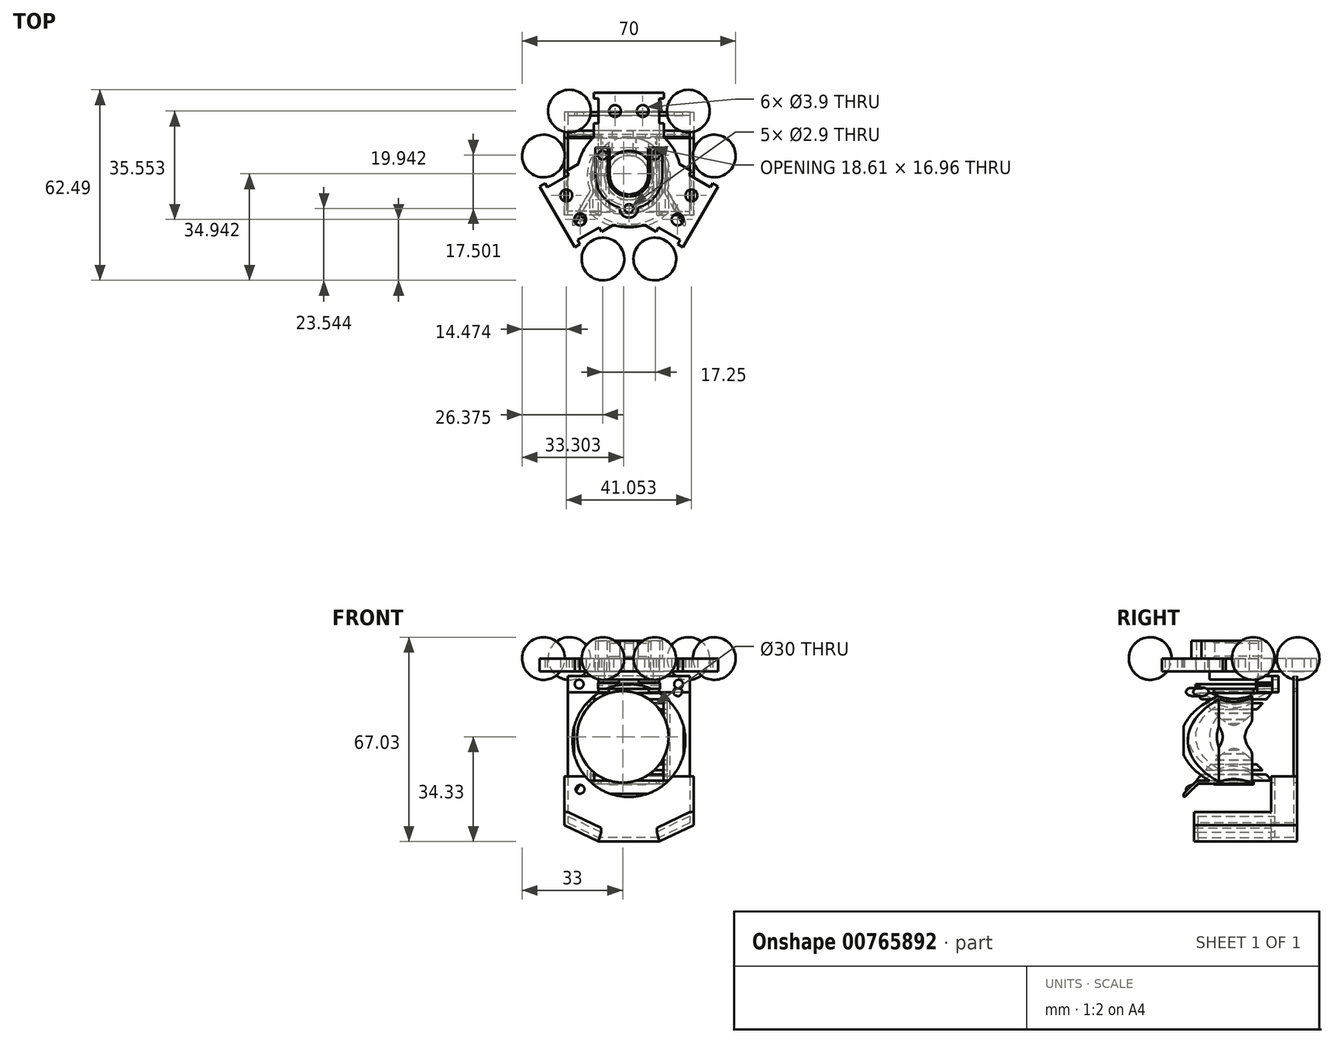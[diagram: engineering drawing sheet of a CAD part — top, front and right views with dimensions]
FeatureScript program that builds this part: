
annotation { "Feature Type Name" : "Feature", "Feature Type Description" : "" }
export const myFeature = defineFeature(function(context is Context, id is Id, definition is map)
    precondition{}
    {
        {
            var Q0;
            Q0=qCreatedBy(makeId("Top.planeOp"),FACE);
            var sketch = newSketch(context, id + "F0", { "sketchPlane" : qUnion([Q0])});
            skCircle(sketch, "E0", {"center": v(0, 0) * mm, "radius": 8.07 * mm});
            skCircle(sketch, "E1", {"center": v(0, 0) * mm, "radius": 17 * mm});
            skLineSegment(sketch, "E2.bottom", {"start": v(-11.5, 17) * mm, "end": v(11.5, 17) * mm});
            skLineSegment(sketch, "E2.top", {"start": v(-11.5, 12.52) * mm, "end": v(11.5, 12.52) * mm});
            skLineSegment(sketch, "E2.left", {"start": v(-11.5, 17) * mm, "end": v(-11.5, 12.52) * mm});
            skLineSegment(sketch, "E2.right", {"start": v(11.5, 17) * mm, "end": v(11.5, 12.52) * mm});
            skLineSegment(sketch, "E3.bottom", {"start": v(-11.5, 27.15) * mm, "end": v(11.5, 27.15) * mm});
            skLineSegment(sketch, "E3.top", {"start": v(-11.5, 25.15) * mm, "end": v(11.5, 25.15) * mm});
            skLineSegment(sketch, "E3.left", {"start": v(-11.5, 27.15) * mm, "end": v(-11.5, 25.15) * mm});
            skLineSegment(sketch, "E3.right", {"start": v(11.5, 27.15) * mm, "end": v(11.5, 25.15) * mm});
            skLineSegment(sketch, "E4.bottom", {"start": v(-9.95, 25.15) * mm, "end": v(9.95, 25.15) * mm});
            skLineSegment(sketch, "E4.top", {"start": v(-9.95, 17) * mm, "end": v(9.95, 17) * mm});
            skLineSegment(sketch, "E4.left", {"start": v(-9.95, 25.15) * mm, "end": v(-9.95, 17) * mm});
            skLineSegment(sketch, "E4.right", {"start": v(9.95, 25.15) * mm, "end": v(9.95, 17) * mm});
            skCircle(sketch, "E5", {"center": v(-4.55, 21.08) * mm, "radius": 1.95 * mm});
            skPoint(sketch, "E6", {"position": v(-9.95, 21.08) * mm});
            skCircle(sketch, "E7.MirrorC", {"center": v(4.55, 21.08) * mm, "radius": 1.95 * mm});
            skLineSegment(sketch, "E8.1.0", {"start": v(-17.76, -23.53) * mm, "end": v(-29.26, -3.62) * mm});
            skLineSegment(sketch, "E8.1.1", {"start": v(-20.47, 1.46) * mm, "end": v(-16.6, 3.7) * mm});
            skCircle(sketch, "E8.1.2", {"center": v(-20.53, -6.6) * mm, "radius": 1.95 * mm});
            skLineSegment(sketch, "E8.1.3", {"start": v(-8.97, -18.46) * mm, "end": v(-5.1, -16.22) * mm});
            skLineSegment(sketch, "E8.1.4", {"start": v(-5.1, -16.22) * mm, "end": v(-16.6, 3.7) * mm});
            skLineSegment(sketch, "E8.1.5", {"start": v(-16.8, -21.2) * mm, "end": v(-26.76, -3.96) * mm});
            skCircle(sketch, "E8.1.6", {"center": v(-15.98, -14.48) * mm, "radius": 1.95 * mm});
            skLineSegment(sketch, "E8.1.7", {"start": v(-26.76, -3.96) * mm, "end": v(-19.7, 0.12) * mm});
            skLineSegment(sketch, "E8.1.8", {"start": v(-16.8, -21.2) * mm, "end": v(-9.75, -17.12) * mm});
            skLineSegment(sketch, "E8.1.9", {"start": v(-9.75, -17.12) * mm, "end": v(-19.7, 0.12) * mm});
            skPoint(sketch, "E8.1.10", {"position": v(-13.28, -19.15) * mm});
            skLineSegment(sketch, "E8.1.11", {"start": v(-16.03, -22.53) * mm, "end": v(-27.53, -2.62) * mm});
            skLineSegment(sketch, "E8.1.12", {"start": v(-8.97, -18.46) * mm, "end": v(-20.47, 1.46) * mm});
            skLineSegment(sketch, "E8.1.13", {"start": v(-17.76, -23.53) * mm, "end": v(-16.03, -22.53) * mm});
            skLineSegment(sketch, "E8.1.14", {"start": v(-29.26, -3.62) * mm, "end": v(-27.53, -2.62) * mm});
            skLineSegment(sketch, "E8.2.0", {"start": v(29.26, -3.62) * mm, "end": v(17.76, -23.53) * mm});
            skLineSegment(sketch, "E8.2.1", {"start": v(8.97, -18.46) * mm, "end": v(5.1, -16.22) * mm});
            skCircle(sketch, "E8.2.2", {"center": v(15.98, -14.48) * mm, "radius": 1.95 * mm});
            skLineSegment(sketch, "E8.2.3", {"start": v(20.47, 1.46) * mm, "end": v(16.6, 3.7) * mm});
            skLineSegment(sketch, "E8.2.4", {"start": v(16.6, 3.7) * mm, "end": v(5.1, -16.22) * mm});
            skLineSegment(sketch, "E8.2.5", {"start": v(26.76, -3.96) * mm, "end": v(16.8, -21.2) * mm});
            skCircle(sketch, "E8.2.6", {"center": v(20.53, -6.6) * mm, "radius": 1.95 * mm});
            skLineSegment(sketch, "E8.2.7", {"start": v(16.8, -21.2) * mm, "end": v(9.75, -17.12) * mm});
            skLineSegment(sketch, "E8.2.8", {"start": v(26.76, -3.96) * mm, "end": v(19.7, 0.12) * mm});
            skLineSegment(sketch, "E8.2.9", {"start": v(19.7, 0.12) * mm, "end": v(9.75, -17.12) * mm});
            skPoint(sketch, "E8.2.10", {"position": v(23.23, -1.92) * mm});
            skLineSegment(sketch, "E8.2.11", {"start": v(27.53, -2.62) * mm, "end": v(16.03, -22.53) * mm});
            skLineSegment(sketch, "E8.2.12", {"start": v(20.47, 1.46) * mm, "end": v(8.97, -18.46) * mm});
            skLineSegment(sketch, "E8.2.13", {"start": v(29.26, -3.62) * mm, "end": v(27.53, -2.62) * mm});
            skLineSegment(sketch, "E8.2.14", {"start": v(17.76, -23.53) * mm, "end": v(16.03, -22.53) * mm});
            skSolve(sketch);
        }
        {
            var Q0;
            Q0 = qSketchRegion(id + "F0", true);
            extrude(context, id + "F1", {"entities" : qUnion([Q0]), "depth" : 4.2 * mm, "offsetDistance" : 25 * mm});
        }
        {
            var Q0;
            Q0=makeQuery(id+"F1.opExtrude","CAP_FACE",FACE,{"disambiguationData":[OSD([sQuery(id+"F0.wireOp",EDGE,"E0"),sQuery(id+"F0.wireOp",EDGE,"E1"),sQuery(id+"F0.wireOp",EDGE,"E2.bottom"),sQuery(id+"F0.wireOp",EDGE,"E2.left"),sQuery(id+"F0.wireOp",EDGE,"E2.right"),sQuery(id+"F0.wireOp",EDGE,"E3.bottom"),sQuery(id+"F0.wireOp",EDGE,"E3.top"),sQuery(id+"F0.wireOp",EDGE,"E3.left"),sQuery(id+"F0.wireOp",EDGE,"E3.right"),sQuery(id+"F0.wireOp",EDGE,"E4.left"),sQuery(id+"F0.wireOp",EDGE,"E4.right"),sQuery(id+"F0.wireOp",EDGE,"E5"),sQuery(id+"F0.wireOp",EDGE,"E7.MirrorC"),sQuery(id+"F0.wireOp",EDGE,"E8.1.0"),sQuery(id+"F0.wireOp",EDGE,"E8.1.1"),sQuery(id+"F0.wireOp",EDGE,"E8.1.2"),sQuery(id+"F0.wireOp",EDGE,"E8.1.3"),sQuery(id+"F0.wireOp",EDGE,"E8.1.6"),sQuery(id+"F0.wireOp",EDGE,"E8.1.7"),sQuery(id+"F0.wireOp",EDGE,"E8.1.8"),sQuery(id+"F0.wireOp",EDGE,"E8.1.11"),sQuery(id+"F0.wireOp",EDGE,"E8.1.12"),sQuery(id+"F0.wireOp",EDGE,"E8.1.13"),sQuery(id+"F0.wireOp",EDGE,"E8.1.14"),sQuery(id+"F0.wireOp",EDGE,"E8.2.0"),sQuery(id+"F0.wireOp",EDGE,"E8.2.1"),sQuery(id+"F0.wireOp",EDGE,"E8.2.2"),sQuery(id+"F0.wireOp",EDGE,"E8.2.3"),sQuery(id+"F0.wireOp",EDGE,"E8.2.6"),sQuery(id+"F0.wireOp",EDGE,"E8.2.7"),sQuery(id+"F0.wireOp",EDGE,"E8.2.8"),sQuery(id+"F0.wireOp",EDGE,"E8.2.11"),sQuery(id+"F0.wireOp",EDGE,"E8.2.12"),sQuery(id+"F0.wireOp",EDGE,"E8.2.13"),sQuery(id+"F0.wireOp",EDGE,"E8.2.14")])],"isStart":false});
            var sketch = newSketch(context, id + "F2", { "sketchPlane" : qUnion([Q0])});
            skArc(sketch, "E9.0", {"start": v(-8.07, 0) * mm, "mid": v(0, -8.07) * mm, "end": v(8.07, 0) * mm, "construction": true});
            skArc(sketch, "E10.0", {"start": v(-11, 0) * mm, "mid": v(0, -11) * mm, "end": v(11, 0) * mm});
            skLineSegment(sketch, "E11", {"start": v(-11, 0) * mm, "end": v(11, 0) * mm, "construction": true});
            skArc(sketch, "E12", {"start": v(-6.25, 0) * mm, "mid": v(0, -6.25) * mm, "end": v(6.25, 0) * mm});
            skLineSegment(sketch, "E13.bottom", {"start": v(-11, 0) * mm, "end": v(-6.25, 0) * mm});
            skLineSegment(sketch, "E13.top", {"start": v(-11, 9) * mm, "end": v(-6.25, 9) * mm});
            skLineSegment(sketch, "E13.left", {"start": v(-11, 0) * mm, "end": v(-11, 9) * mm});
            skLineSegment(sketch, "E13.right", {"start": v(-6.25, 0) * mm, "end": v(-6.25, 9) * mm});
            skLineSegment(sketch, "E14.MirrorCS", {"start": v(11, 0) * mm, "end": v(11, 9) * mm});
            skLineSegment(sketch, "E15.MirrorCS", {"start": v(6.25, 0) * mm, "end": v(6.25, 9) * mm});
            skLineSegment(sketch, "E16.MirrorCS", {"start": v(11, 9) * mm, "end": v(6.25, 9) * mm});
            skCircle(sketch, "E17", {"center": v(8.62, 6.63) * mm, "radius": 1.45 * mm});
            skPoint(sketch, "E17.centerSnap0", {"position": v(8.62, 9) * mm});
            skCircle(sketch, "E18", {"center": v(8.62, 6.63) * mm, "radius": 2.37 * mm, "construction": true});
            skCircle(sketch, "E19.MirrorC", {"center": v(-8.62, 6.63) * mm, "radius": 1.45 * mm});
            skCircle(sketch, "E20", {"center": v(0, 0) * mm, "radius": 10.88 * mm, "construction": true});
            skCircle(sketch, "E21", {"center": v(0, -10.88) * mm, "radius": 1.45 * mm});
            skPoint(sketch, "E21.centerSnap0", {"position": v(0, -11) * mm});
            skCircle(sketch, "E22", {"center": v(0, -10.88) * mm, "radius": 3 * mm});
            skSolve(sketch);
        }
        {
            var Q0;
            Q0 = qSketchRegion(id + "F2", true);
            extrude(context, id + "F3", {"entities" : qUnion([Q0]), "depth" : 5.8 * mm, "offsetDistance" : 25 * mm});
        }
        {
            var Q0;
            Q0=makeQuery(id+"F2.imprint","IMPRINT",FACE,{"disambiguationData":[TD([[makeQuery(id+"F2.imprint","IMPRINT",EDGE,{"derivedFrom":sQuery(id+"F2.wireOp",EDGE,"E19.MirrorC")}),-1.0]])]});
            var Q1;
            Q1=makeQuery(id+"F2.imprint","IMPRINT",FACE,{"disambiguationData":[TD([[makeQuery(id+"F2.imprint","IMPRINT",EDGE,{"derivedFrom":sQuery(id+"F2.wireOp",EDGE,"E17")}),1.0]])]});
            var Q2;
            {var subQ0=sQuery(id+"F2.wireOp",EDGE,"E21");var subQ1=sQuery(id+"F2.wireOp",EDGE,"E10.0");var subQ2=makeQuery(id+"F2.imprint","INTERSECT",VERTEX,{"disambiguationData":[OD(0.0)],"derivedFrom":[subQ1,subQ0]});Q2=makeQuery(id+"F2.imprint","IMPRINT",FACE,{"disambiguationData":[TD([[makeQuery(id+"F2.imprint","IMPRINT",EDGE,{"disambiguationData":[TD([[subQ2,-1.0]])],"derivedFrom":subQ1}),1.0]])]});}
            var Q3;
            {var subQ0=sQuery(id+"F2.wireOp",EDGE,"E21");var subQ1=sQuery(id+"F2.wireOp",EDGE,"E10.0");var subQ2=makeQuery(id+"F2.imprint","INTERSECT",VERTEX,{"disambiguationData":[OD(0.0)],"derivedFrom":[subQ1,subQ0]});Q3=makeQuery(id+"F2.imprint","IMPRINT",FACE,{"disambiguationData":[TD([[makeQuery(id+"F2.imprint","IMPRINT",EDGE,{"disambiguationData":[TD([[subQ2,-1.0]])],"derivedFrom":subQ1}),-1.0]])]});}
            extrude(context, id + "F4", {"entities" : qUnion([Q0, Q1, Q2, Q3]), "operationType" : NewBodyOperationType.REMOVE, "endBound" : BoundingType.THROUGH_ALL, "oppositeDirection" : true, "depth" : 25 * mm, "offsetDistance" : 25 * mm});
        }
        {
            var Q0;
            Q0=makeQuery(id+"F1.opExtrude","CAP_FACE",FACE,{"disambiguationData":[OSD([sQuery(id+"F0.wireOp",EDGE,"E0"),sQuery(id+"F0.wireOp",EDGE,"E1"),sQuery(id+"F0.wireOp",EDGE,"E2.bottom"),sQuery(id+"F0.wireOp",EDGE,"E2.left"),sQuery(id+"F0.wireOp",EDGE,"E2.right"),sQuery(id+"F0.wireOp",EDGE,"E3.bottom"),sQuery(id+"F0.wireOp",EDGE,"E3.top"),sQuery(id+"F0.wireOp",EDGE,"E3.left"),sQuery(id+"F0.wireOp",EDGE,"E3.right"),sQuery(id+"F0.wireOp",EDGE,"E4.left"),sQuery(id+"F0.wireOp",EDGE,"E4.right"),sQuery(id+"F0.wireOp",EDGE,"E5"),sQuery(id+"F0.wireOp",EDGE,"E7.MirrorC"),sQuery(id+"F0.wireOp",EDGE,"E8.1.0"),sQuery(id+"F0.wireOp",EDGE,"E8.1.1"),sQuery(id+"F0.wireOp",EDGE,"E8.1.2"),sQuery(id+"F0.wireOp",EDGE,"E8.1.3"),sQuery(id+"F0.wireOp",EDGE,"E8.1.6"),sQuery(id+"F0.wireOp",EDGE,"E8.1.7"),sQuery(id+"F0.wireOp",EDGE,"E8.1.8"),sQuery(id+"F0.wireOp",EDGE,"E8.1.11"),sQuery(id+"F0.wireOp",EDGE,"E8.1.12"),sQuery(id+"F0.wireOp",EDGE,"E8.1.13"),sQuery(id+"F0.wireOp",EDGE,"E8.1.14"),sQuery(id+"F0.wireOp",EDGE,"E8.2.0"),sQuery(id+"F0.wireOp",EDGE,"E8.2.1"),sQuery(id+"F0.wireOp",EDGE,"E8.2.2"),sQuery(id+"F0.wireOp",EDGE,"E8.2.3"),sQuery(id+"F0.wireOp",EDGE,"E8.2.6"),sQuery(id+"F0.wireOp",EDGE,"E8.2.7"),sQuery(id+"F0.wireOp",EDGE,"E8.2.8"),sQuery(id+"F0.wireOp",EDGE,"E8.2.11"),sQuery(id+"F0.wireOp",EDGE,"E8.2.12"),sQuery(id+"F0.wireOp",EDGE,"E8.2.13"),sQuery(id+"F0.wireOp",EDGE,"E8.2.14")])],"isStart":false});
            var sketch = newSketch(context, id + "F5", { "sketchPlane" : qUnion([Q0])});
            skLineSegment(sketch, "E23.bottom", {"start": v(11.5, 25.15) * mm, "end": v(19.5, 25.15) * mm});
            skLineSegment(sketch, "E23.top", {"start": v(11.5, 17) * mm, "end": v(19.5, 17) * mm});
            skLineSegment(sketch, "E23.left", {"start": v(11.5, 25.15) * mm, "end": v(11.5, 17) * mm});
            skLineSegment(sketch, "E23.right", {"start": v(19.5, 25.15) * mm, "end": v(19.5, 17) * mm});
            skCircle(sketch, "E24", {"center": v(19.5, 21.08) * mm, "radius": 7 * mm});
            skLineSegment(sketch, "E25", {"start": v(19.5, 28.08) * mm, "end": v(19.5, 14.08) * mm});
            skLineSegment(sketch, "E26.MirrorCS", {"start": v(-19.5, 28.08) * mm, "end": v(-19.5, 14.08) * mm});
            skArc(sketch, "E27.MirrorC", {"start": v(-19.5, 14.08) * mm, "mid": v(-26.5, 21.08) * mm, "end": v(-19.5, 28.08) * mm});
            skSolve(sketch);
        }
        {
            var Q0;
            {var subQ0=sQuery(id+"F5.wireOp",EDGE,"E23.right");Q0=makeQuery(id+"F5.imprint","IMPRINT",FACE,{"disambiguationData":[TD([[makeQuery(id+"F5.imprint","IMPRINT",EDGE,{"derivedFrom":subQ0}),1.0]])]});}
            var Q1;
            Q1=sQuery(id+"F5.wireOp",EDGE,"E23.right");
            revolve(context, id + "F6", {"surfaceOperationType" : NewSurfaceOperationType.NEW, "entities" : qUnion([Q0]), "axis" : qUnion([Q1]), "revolveType" : RevolveType.FULL});
        }
        {
            var Q0;
            Q0=makeQuery(id+"F5.imprint","IMPRINT",FACE,{"disambiguationData":[TD([[makeQuery(id+"F5.imprint","IMPRINT",EDGE,{"derivedFrom":sQuery(id+"F5.wireOp",EDGE,"E26.MirrorCS")}),-1.0]])]});
            var Q1;
            Q1=sQuery(id+"F5.wireOp",EDGE,"E26.MirrorCS");
            revolve(context, id + "F7", {"surfaceOperationType" : NewSurfaceOperationType.NEW, "entities" : qUnion([Q0]), "axis" : qUnion([Q1]), "revolveType" : RevolveType.FULL});
        }
        {
            var Q0;
            Q0=makeQuery(id+"F6.opRevolve","SWEPT_BODY",BODY,{"disambiguationData":[OSD([sQuery(id+"F5.wireOp",EDGE,"E23.right"),sQuery(id+"F5.wireOp",EDGE,"E24"),sQuery(id+"F5.wireOp",EDGE,"E25")])]});
            var Q1;
            Q1=makeQuery(id+"F7.opRevolve","SWEPT_BODY",BODY,{"disambiguationData":[OSD([sQuery(id+"F5.wireOp",EDGE,"E26.MirrorCS"),sQuery(id+"F5.wireOp",EDGE,"E27.MirrorC")])]});
            var Q2;
            Q2=makeQuery(id+"F1.opExtrude","CAP_EDGE",EDGE,{"disambiguationData":[OSD([sQuery(id+"F0.wireOp",EDGE,"E0")])],"isStart":false});
            circularPattern(context, id + "F8", {"entities" : qUnion([Q0, Q1]), "axis" : qUnion([Q2]), "angle" : 360 * degree, "instanceCount" : 3, "equalSpace" : true});
        }
        {
            var Q0;
            Q0=makeQuery(id+"F1.opExtrude","CAP_FACE",FACE,{"disambiguationData":[OSD([sQuery(id+"F0.wireOp",EDGE,"E0"),sQuery(id+"F0.wireOp",EDGE,"E1"),sQuery(id+"F0.wireOp",EDGE,"E2.bottom"),sQuery(id+"F0.wireOp",EDGE,"E2.left"),sQuery(id+"F0.wireOp",EDGE,"E2.right"),sQuery(id+"F0.wireOp",EDGE,"E3.bottom"),sQuery(id+"F0.wireOp",EDGE,"E3.top"),sQuery(id+"F0.wireOp",EDGE,"E3.left"),sQuery(id+"F0.wireOp",EDGE,"E3.right"),sQuery(id+"F0.wireOp",EDGE,"E4.left"),sQuery(id+"F0.wireOp",EDGE,"E4.right"),sQuery(id+"F0.wireOp",EDGE,"E5"),sQuery(id+"F0.wireOp",EDGE,"E7.MirrorC"),sQuery(id+"F0.wireOp",EDGE,"E8.1.0"),sQuery(id+"F0.wireOp",EDGE,"E8.1.1"),sQuery(id+"F0.wireOp",EDGE,"E8.1.2"),sQuery(id+"F0.wireOp",EDGE,"E8.1.3"),sQuery(id+"F0.wireOp",EDGE,"E8.1.6"),sQuery(id+"F0.wireOp",EDGE,"E8.1.7"),sQuery(id+"F0.wireOp",EDGE,"E8.1.8"),sQuery(id+"F0.wireOp",EDGE,"E8.1.11"),sQuery(id+"F0.wireOp",EDGE,"E8.1.12"),sQuery(id+"F0.wireOp",EDGE,"E8.1.13"),sQuery(id+"F0.wireOp",EDGE,"E8.1.14"),sQuery(id+"F0.wireOp",EDGE,"E8.2.0"),sQuery(id+"F0.wireOp",EDGE,"E8.2.1"),sQuery(id+"F0.wireOp",EDGE,"E8.2.2"),sQuery(id+"F0.wireOp",EDGE,"E8.2.3"),sQuery(id+"F0.wireOp",EDGE,"E8.2.6"),sQuery(id+"F0.wireOp",EDGE,"E8.2.7"),sQuery(id+"F0.wireOp",EDGE,"E8.2.8"),sQuery(id+"F0.wireOp",EDGE,"E8.2.11"),sQuery(id+"F0.wireOp",EDGE,"E8.2.12"),sQuery(id+"F0.wireOp",EDGE,"E8.2.13"),sQuery(id+"F0.wireOp",EDGE,"E8.2.14")])],"isStart":false});
            var sketch = newSketch(context, id + "F9", { "sketchPlane" : qUnion([Q0])});
            skCircle(sketch, "E28", {"center": v(0, 0) * mm, "radius": 8 * mm});
            skSolve(sketch);
        }
        {
            var Q0;
            Q0 = qSketchRegion(id + "F9", true);
            extrude(context, id + "F10", {"entities" : qUnion([Q0]), "oppositeDirection" : true, "depth" : 8 * mm, "offsetDistance" : 25 * mm});
        }
        {
            var Q0;
            Q0=qCreatedBy(makeId("Front.planeOp"),FACE);
            var sketch = newSketch(context, id + "F11", { "sketchPlane" : qUnion([Q0])});
            skLineSegment(sketch, "E29", {"start": v(0, -3.8) * mm, "end": v(-12.5, -3.8) * mm});
            skLineSegment(sketch, "E30", {"start": v(-12.5, -3.8) * mm, "end": v(-12.5, -5.8) * mm});
            skLineSegment(sketch, "E31", {"start": v(-12.5, -5.8) * mm, "end": v(-6.5, -5.8) * mm});
            skLineSegment(sketch, "E32", {"start": v(-6.5, -5.8) * mm, "end": v(-6.5, -7.13) * mm});
            skLineSegment(sketch, "E33.0.1.0", {"start": v(-6.5, -9.13) * mm, "end": v(-6.5, -10.47) * mm});
            skLineSegment(sketch, "E33.0.1.1", {"start": v(-12.5, -9.13) * mm, "end": v(-6.5, -9.13) * mm});
            skLineSegment(sketch, "E33.0.1.2", {"start": v(0, -7.13) * mm, "end": v(-12.5, -7.13) * mm});
            skLineSegment(sketch, "E33.0.1.3", {"start": v(-12.5, -7.13) * mm, "end": v(-12.5, -9.13) * mm});
            skLineSegment(sketch, "E33.0.2.0", {"start": v(-6.5, -12.47) * mm, "end": v(-6.5, -13.8) * mm});
            skLineSegment(sketch, "E33.0.2.1", {"start": v(-12.5, -12.47) * mm, "end": v(-6.5, -12.47) * mm});
            skLineSegment(sketch, "E33.0.2.2", {"start": v(0, -10.47) * mm, "end": v(-12.5, -10.47) * mm});
            skLineSegment(sketch, "E33.0.2.3", {"start": v(-12.5, -10.47) * mm, "end": v(-12.5, -12.47) * mm});
            skLineSegment(sketch, "E33.0.3.0", {"start": v(-6.5, -15.8) * mm, "end": v(-6.5, -17.13) * mm});
            skLineSegment(sketch, "E33.0.3.1", {"start": v(-12.5, -15.8) * mm, "end": v(-6.5, -15.8) * mm});
            skLineSegment(sketch, "E33.0.3.2", {"start": v(0, -13.8) * mm, "end": v(-12.5, -13.8) * mm});
            skLineSegment(sketch, "E33.0.3.3", {"start": v(-12.5, -13.8) * mm, "end": v(-12.5, -15.8) * mm});
            skLineSegment(sketch, "E33.0.4.0", {"start": v(-6.5, -19.13) * mm, "end": v(-6.5, -20.47) * mm});
            skLineSegment(sketch, "E33.0.4.1", {"start": v(-12.5, -19.13) * mm, "end": v(-6.5, -19.13) * mm});
            skLineSegment(sketch, "E33.0.4.2", {"start": v(0, -17.13) * mm, "end": v(-12.5, -17.13) * mm});
            skLineSegment(sketch, "E33.0.4.3", {"start": v(-12.5, -17.13) * mm, "end": v(-12.5, -19.13) * mm});
            skLineSegment(sketch, "E33.0.5.0", {"start": v(-6.5, -22.47) * mm, "end": v(-6.5, -23.8) * mm});
            skLineSegment(sketch, "E33.0.5.1", {"start": v(-12.5, -22.47) * mm, "end": v(-6.5, -22.47) * mm});
            skLineSegment(sketch, "E33.0.5.2", {"start": v(0, -20.47) * mm, "end": v(-12.5, -20.47) * mm});
            skLineSegment(sketch, "E33.0.5.3", {"start": v(-12.5, -20.47) * mm, "end": v(-12.5, -22.47) * mm});
            skLineSegment(sketch, "E33.0.6.0", {"start": v(-6.5, -25.8) * mm, "end": v(-6.5, -27.13) * mm});
            skLineSegment(sketch, "E33.0.6.1", {"start": v(-12.5, -25.8) * mm, "end": v(-6.5, -25.8) * mm});
            skLineSegment(sketch, "E33.0.6.2", {"start": v(0, -23.8) * mm, "end": v(-12.5, -23.8) * mm});
            skLineSegment(sketch, "E33.0.6.3", {"start": v(-12.5, -23.8) * mm, "end": v(-12.5, -25.8) * mm});
            skLineSegment(sketch, "E33.0.7.0", {"start": v(-6.5, -29.13) * mm, "end": v(-6.5, -30.47) * mm});
            skLineSegment(sketch, "E33.0.7.1", {"start": v(-12.5, -29.13) * mm, "end": v(-6.5, -29.13) * mm});
            skLineSegment(sketch, "E33.0.7.2", {"start": v(0, -27.13) * mm, "end": v(-12.5, -27.13) * mm});
            skLineSegment(sketch, "E33.0.7.3", {"start": v(-12.5, -27.13) * mm, "end": v(-12.5, -29.13) * mm});
            skLineSegment(sketch, "E33.0.8.0", {"start": v(-6.5, -32.47) * mm, "end": v(-6.5, -33.8) * mm});
            skLineSegment(sketch, "E33.0.8.1", {"start": v(-12.5, -32.47) * mm, "end": v(-6.5, -32.47) * mm});
            skLineSegment(sketch, "E33.0.8.2", {"start": v(0, -30.47) * mm, "end": v(-12.5, -30.47) * mm});
            skLineSegment(sketch, "E33.0.8.3", {"start": v(-12.5, -30.47) * mm, "end": v(-12.5, -32.47) * mm});
            skLineSegment(sketch, "E33.0.9.0", {"start": v(-6.5, -35.8) * mm, "end": v(-6.5, -37.13) * mm});
            skLineSegment(sketch, "E33.0.9.1", {"start": v(-12.5, -35.8) * mm, "end": v(-6.5, -35.8) * mm});
            skLineSegment(sketch, "E33.0.9.2", {"start": v(0, -33.8) * mm, "end": v(-12.5, -33.8) * mm});
            skLineSegment(sketch, "E33.0.9.3", {"start": v(-12.5, -33.8) * mm, "end": v(-12.5, -35.8) * mm});
            skLineSegment(sketch, "E33.direction1", {"start": v(-12.5, -5.8) * mm, "end": v(12.5, -5.8) * mm, "construction": true});
            skLineSegment(sketch, "E33.direction2", {"start": v(-12.5, -5.8) * mm, "end": v(-12.5, -9.13) * mm, "construction": true});
            skLineSegment(sketch, "E34", {"start": v(-6.5, -37.13) * mm, "end": v(0, -37.13) * mm});
            skLineSegment(sketch, "E35", {"start": v(0, -3.8) * mm, "end": v(0, -37.13) * mm});
            skSolve(sketch);
        }
        {
            var Q0;
            Q0 = qSketchRegion(id + "F11", true);
            var Q1;
            Q1=makeQuery(id+"F10.opExtrude","CAP_EDGE",EDGE,{"disambiguationData":[OSD([sQuery(id+"F9.wireOp",EDGE,"E28")])],"isStart":false});
            revolve(context, id + "F12", {"operationType" : NewBodyOperationType.ADD, "surfaceOperationType" : NewSurfaceOperationType.NEW, "entities" : qUnion([Q0]), "axis" : qUnion([Q1]), "revolveType" : RevolveType.FULL});
        }
        {
            var Q0;
            Q0=makeQuery(id+"F12.opRevolve","SWEPT_FACE",FACE,{"disambiguationData":[OSD([sQuery(id+"F11.wireOp",EDGE,"E33.0.9.1")])]});
            var Q1;
            Q1=makeQuery(id+"F12.opRevolve","SWEPT_FACE",FACE,{"disambiguationData":[OSD([sQuery(id+"F11.wireOp",EDGE,"E29")])]});
            cPlane(context, id + "F13", {"entities" : qUnion([Q0, Q1]), "cplaneType" : CPlaneType.MID_PLANE, "offset" : 15 * mm, "oppositeDirection" : true, "width" : 150 * mm, "height" : 150 * mm});
        }
        {
            var Q0;
            Q0=qCreatedBy(id+"F13.planeOp",FACE);
            var sketch = newSketch(context, id + "F14", { "sketchPlane" : qUnion([Q0])});
            skArc(sketch, "E36", {"start": v(11.33, -5.28) * mm, "mid": v(12.5, -0.06) * mm, "end": v(11.38, 5.17) * mm});
            skLineSegment(sketch, "E37", {"start": v(11.33, -5.28) * mm, "end": v(0, 0) * mm, "construction": true});
            skArc(sketch, "E38.0", {"start": v(12.24, -5.7) * mm, "mid": v(13.5, -0.45) * mm, "end": v(12.6, 4.87) * mm});
            skLineSegment(sketch, "E39", {"start": v(-20, 17.7) * mm, "end": v(20, 17.7) * mm});
            skLineSegment(sketch, "E40", {"start": v(20, 17.7) * mm, "end": v(12.6, 4.87) * mm});
            skLineSegment(sketch, "E41.MirrorCS", {"start": v(-20, 17.7) * mm, "end": v(-12.6, 4.87) * mm});
            skArc(sketch, "E42.trimOffspring", {"start": v(-12.6, 4.87) * mm, "mid": v(-13.5, -0.45) * mm, "end": v(-12.24, -5.7) * mm});
            skLineSegment(sketch, "E43.0", {"start": v(-17.92, 16.5) * mm, "end": v(-11.38, 5.17) * mm});
            skLineSegment(sketch, "E43.1", {"start": v(-17.92, 16.5) * mm, "end": v(17.92, 16.5) * mm});
            skLineSegment(sketch, "E43.2", {"start": v(17.92, 16.5) * mm, "end": v(11.38, 5.17) * mm});
            skArc(sketch, "E44.trimOffspring", {"start": v(-11.38, 5.17) * mm, "mid": v(-12.5, -0.06) * mm, "end": v(-11.33, -5.28) * mm});
            skLineSegment(sketch, "E45", {"start": v(12.24, -5.7) * mm, "end": v(11.33, -5.28) * mm, "construction": true});
            skArc(sketch, "E46", {"start": v(11.33, -5.28) * mm, "mid": v(11.57, -5.95) * mm, "end": v(12.24, -5.7) * mm});
            skArc(sketch, "E47.MirrorCS", {"start": v(-11.33, -5.28) * mm, "mid": v(-11.57, -5.95) * mm, "end": v(-12.24, -5.7) * mm});
            skSolve(sketch);
        }
        {
            var Q0;
            Q0 = qSketchRegion(id + "F14", true);
            extrude(context, id + "F15", {"entities" : qUnion([Q0]), "endBound" : BoundingType.SYMMETRIC, "oppositeDirection" : true, "depth" : 32.2 * mm, "offsetDistance" : 25 * mm});
        }
        {
            var Q0;
            Q0=makeQuery(id+"F15.opExtrude","CAP_FACE",FACE,{"disambiguationData":[OSD([sQuery(id+"F14.wireOp",EDGE,"E36"),sQuery(id+"F14.wireOp",EDGE,"E38.0"),sQuery(id+"F14.wireOp",EDGE,"E39"),sQuery(id+"F14.wireOp",EDGE,"E40"),sQuery(id+"F14.wireOp",EDGE,"E41.MirrorCS"),sQuery(id+"F14.wireOp",EDGE,"E42.trimOffspring"),sQuery(id+"F14.wireOp",EDGE,"E43.0"),sQuery(id+"F14.wireOp",EDGE,"E43.1"),sQuery(id+"F14.wireOp",EDGE,"E43.2"),sQuery(id+"F14.wireOp",EDGE,"E44.trimOffspring"),sQuery(id+"F14.wireOp",EDGE,"E46"),sQuery(id+"F14.wireOp",EDGE,"E47.MirrorCS")])],"isStart":false});
            var sketch = newSketch(context, id + "F16", { "sketchPlane" : qUnion([Q0])});
            skArc(sketch, "E48.0.0", {"start": v(-12.24, 5.7) * mm, "mid": v(-11.57, 5.95) * mm, "end": v(-11.33, 5.28) * mm});
            skArc(sketch, "E48.0.1", {"start": v(-11.33, 5.28) * mm, "mid": v(-12.5, 0.06) * mm, "end": v(-11.38, -5.17) * mm});
            skArc(sketch, "E48.0.5", {"start": v(11.38, -5.17) * mm, "mid": v(12.5, 0.06) * mm, "end": v(11.33, 5.28) * mm});
            skArc(sketch, "E48.0.6", {"start": v(11.33, 5.28) * mm, "mid": v(11.57, 5.95) * mm, "end": v(12.24, 5.7) * mm});
            skArc(sketch, "E48.0.7", {"start": v(12.24, 5.7) * mm, "mid": v(13.5, 0.45) * mm, "end": v(12.6, -4.87) * mm});
            skLineSegment(sketch, "E48.0.8", {"start": v(12.6, -4.87) * mm, "end": v(20, -17.7) * mm});
            skLineSegment(sketch, "E48.0.9", {"start": v(20, -17.7) * mm, "end": v(-20, -17.7) * mm});
            skLineSegment(sketch, "E48.0.10", {"start": v(-20, -17.7) * mm, "end": v(-12.6, -4.87) * mm});
            skArc(sketch, "E48.0.11", {"start": v(-12.6, -4.87) * mm, "mid": v(-13.5, 0.45) * mm, "end": v(-12.24, 5.7) * mm});
            skArc(sketch, "E49", {"start": v(-9.06, 4.23) * mm, "mid": v(0, -10) * mm, "end": v(9.06, 4.23) * mm});
            skLineSegment(sketch, "E50", {"start": v(-11.33, 5.28) * mm, "end": v(-9.06, 4.23) * mm});
            skLineSegment(sketch, "E51", {"start": v(9.06, 4.23) * mm, "end": v(11.33, 5.28) * mm});
            skSolve(sketch);
        }
        {
            var Q0;
            Q0 = qSketchRegion(id + "F16", true);
            extrude(context, id + "F17", {"entities" : qUnion([Q0]), "depth" : 1 * mm, "offsetDistance" : 25 * mm});
        }
        {
            var Q0;
            Q0=qCreatedBy(makeId("Right.planeOp"),FACE);
            var sketch = newSketch(context, id + "F18", { "sketchPlane" : qUnion([Q0])});
            skLineSegment(sketch, "E52", {"start": v(-10.7, -35.9) * mm, "end": v(-17.7, -42.7) * mm});
            skLineSegment(sketch, "E53", {"start": v(-17.7, -42.7) * mm, "end": v(-17.7, -35.9) * mm});
            skLineSegment(sketch, "E54", {"start": v(-17.7, -35.9) * mm, "end": v(-10.7, -35.9) * mm});
            skSolve(sketch);
        }
        {
            var Q0;
            Q0=makeQuery(id+"F18.imprint","IMPRINT",FACE,{"disambiguationData":[TD([[makeQuery(id+"F18.imprint","IMPRINT",EDGE,{"derivedFrom":sQuery(id+"F18.wireOp",EDGE,"E52")}),-1.0]])]});
            extrude(context, id + "F19", {"entities" : qUnion([Q0]), "operationType" : NewBodyOperationType.ADD, "endBound" : BoundingType.SYMMETRIC, "depth" : 42 * mm, "offsetDistance" : 25 * mm});
        }
        {
            var Q0;
            Q0=makeQuery(id+"F17.opExtrude","SWEPT_BODY",BODY,{"disambiguationData":[OSD([sQuery(id+"F16.wireOp",EDGE,"E48.0.0"),sQuery(id+"F16.wireOp",EDGE,"E48.0.6"),sQuery(id+"F16.wireOp",EDGE,"E48.0.7"),sQuery(id+"F16.wireOp",EDGE,"E48.0.8"),sQuery(id+"F16.wireOp",EDGE,"E48.0.9"),sQuery(id+"F16.wireOp",EDGE,"E48.0.10"),sQuery(id+"F16.wireOp",EDGE,"E48.0.11"),sQuery(id+"F16.wireOp",EDGE,"E49"),sQuery(id+"F16.wireOp",EDGE,"E50"),sQuery(id+"F16.wireOp",EDGE,"E51")])]});
            var Q1;
            Q1=qCreatedBy(id+"F13.planeOp",FACE);
            mirror(context, id + "F20", {"entities" : qUnion([Q0]), "mirrorPlane" : qUnion([Q1])});
        }
        {
            var Q0;
            {var subQ2=sQuery(id+"F14.wireOp",EDGE,"E41.MirrorCS");var subQ3=sQuery(id+"F18.wireOp",EDGE,"E54");Q0=makeQuery(id+"F19.boolean.opBoolean","SPLIT",FACE,{"disambiguationData":[TD([makeQuery(id+"F15.opExtrude","SWEPT_FACE",FACE,{"disambiguationData":[OSD([subQ2])]})])],"derivedFrom":makeQuery(id+"F19.opExtrude","SWEPT_FACE",FACE,{"disambiguationData":[OSD([subQ3])]})});}
            var Q1;
            {var subQ0=sQuery(id+"F14.wireOp",EDGE,"E40");var subQ3=sQuery(id+"F18.wireOp",EDGE,"E54");Q1=makeQuery(id+"F19.boolean.opBoolean","SPLIT",FACE,{"disambiguationData":[TD([makeQuery(id+"F15.opExtrude","SWEPT_FACE",FACE,{"disambiguationData":[OSD([subQ0])]})])],"derivedFrom":makeQuery(id+"F19.opExtrude","SWEPT_FACE",FACE,{"disambiguationData":[OSD([subQ3])]})});}
            var Q2;
            {var subQ2=sQuery(id+"F14.wireOp",EDGE,"E43.0");Q2=makeQuery(id+"F19.boolean.opBoolean","SPLIT",FACE,{"disambiguationData":[TD([makeQuery(id+"F15.opExtrude","SWEPT_FACE",FACE,{"disambiguationData":[OSD([subQ2])]})])],"derivedFrom":makeQuery(id+"F19.opExtrude","SWEPT_FACE",FACE,{"disambiguationData":[OSD([sQuery(id+"F18.wireOp",EDGE,"E54")])]})});}
            extrude(context, id + "F21", {"entities" : qUnion([Q0, Q1, Q2]), "operationType" : NewBodyOperationType.REMOVE, "endBound" : BoundingType.THROUGH_ALL, "oppositeDirection" : true, "depth" : 25 * mm, "offsetDistance" : 25 * mm});
        }
        {
            var Q0;
            Q0=makeQuery(id+"F20.opPattern","COPY",BODY,{"derivedFrom":makeQuery(id+"F17.opExtrude","SWEPT_BODY",BODY,{"disambiguationData":[OSD([sQuery(id+"F16.wireOp",EDGE,"E48.0.0"),sQuery(id+"F16.wireOp",EDGE,"E48.0.6"),sQuery(id+"F16.wireOp",EDGE,"E48.0.7"),sQuery(id+"F16.wireOp",EDGE,"E48.0.8"),sQuery(id+"F16.wireOp",EDGE,"E48.0.9"),sQuery(id+"F16.wireOp",EDGE,"E48.0.10"),sQuery(id+"F16.wireOp",EDGE,"E48.0.11"),sQuery(id+"F16.wireOp",EDGE,"E49"),sQuery(id+"F16.wireOp",EDGE,"E50"),sQuery(id+"F16.wireOp",EDGE,"E51")])]}),"instanceName":"1"});
            var Q1;
            Q1=makeQuery(id+"F15.opExtrude","SWEPT_BODY",BODY,{"disambiguationData":[OSD([sQuery(id+"F14.wireOp",EDGE,"E36"),sQuery(id+"F14.wireOp",EDGE,"E38.0"),sQuery(id+"F14.wireOp",EDGE,"E39"),sQuery(id+"F14.wireOp",EDGE,"E40"),sQuery(id+"F14.wireOp",EDGE,"E41.MirrorCS"),sQuery(id+"F14.wireOp",EDGE,"E42.trimOffspring"),sQuery(id+"F14.wireOp",EDGE,"E43.0"),sQuery(id+"F14.wireOp",EDGE,"E43.1"),sQuery(id+"F14.wireOp",EDGE,"E43.2"),sQuery(id+"F14.wireOp",EDGE,"E44.trimOffspring"),sQuery(id+"F14.wireOp",EDGE,"E46"),sQuery(id+"F14.wireOp",EDGE,"E47.MirrorCS")])]});
            var Q2;
            Q2=makeQuery(id+"F17.opExtrude","SWEPT_BODY",BODY,{"disambiguationData":[OSD([sQuery(id+"F16.wireOp",EDGE,"E48.0.0"),sQuery(id+"F16.wireOp",EDGE,"E48.0.6"),sQuery(id+"F16.wireOp",EDGE,"E48.0.7"),sQuery(id+"F16.wireOp",EDGE,"E48.0.8"),sQuery(id+"F16.wireOp",EDGE,"E48.0.9"),sQuery(id+"F16.wireOp",EDGE,"E48.0.10"),sQuery(id+"F16.wireOp",EDGE,"E48.0.11"),sQuery(id+"F16.wireOp",EDGE,"E49"),sQuery(id+"F16.wireOp",EDGE,"E50"),sQuery(id+"F16.wireOp",EDGE,"E51")])]});
            booleanBodies(context, id + "F22", {"operationType" : BooleanOperationType.UNION, "tools" : qUnion([Q0, Q1, Q2])});
        }
        {
            var Q0;
            Q0=qCreatedBy(makeId("Right.planeOp"),FACE);
            var sketch = newSketch(context, id + "F23", { "sketchPlane" : qUnion([Q0])});
            skLineSegment(sketch, "E55.0", {"start": v(-11.73, -36.9) * mm, "end": v(-16.5, -41.53) * mm});
            skLineSegment(sketch, "E56.0", {"start": v(-10.7, -36.9) * mm, "end": v(-11.73, -36.9) * mm});
            skLineSegment(sketch, "E57.0", {"start": v(-10.7, -36.9) * mm, "end": v(-10.7, -35.9) * mm});
            skLineSegment(sketch, "E58.0", {"start": v(-12.14, -35.9) * mm, "end": v(-16.5, -40.14) * mm});
            skLineSegment(sketch, "E58.1", {"start": v(-10.7, -35.9) * mm, "end": v(-12.14, -35.9) * mm});
            skLineSegment(sketch, "E59", {"start": v(-16.5, -40.14) * mm, "end": v(-16.5, -41.53) * mm});
            skSolve(sketch);
        }
        {
            var Q0;
            Q0=makeQuery(id+"F23.imprint","IMPRINT",FACE,{"disambiguationData":[TD([[makeQuery(id+"F23.imprint","IMPRINT",EDGE,{"derivedFrom":sQuery(id+"F23.wireOp",EDGE,"E55.0")}),-1.0]])]});
            extrude(context, id + "F24", {"entities" : qUnion([Q0]), "operationType" : NewBodyOperationType.ADD, "endBound" : BoundingType.SYMMETRIC, "depth" : 38 * mm, "offsetDistance" : 25 * mm});
        }
        {
            var Q0;
            {var subQ0=sQuery(id+"F23.wireOp",EDGE,"E58.1");Q0=makeQuery(id+"F24.boolean.opBoolean","SPLIT",FACE,{"disambiguationData":[TD([makeQuery(id+"F15.opExtrude","SWEPT_FACE",FACE,{"disambiguationData":[OSD([sQuery(id+"F14.wireOp",EDGE,"E40")])]})])],"derivedFrom":makeQuery(id+"F24.opExtrude","SWEPT_FACE",FACE,{"disambiguationData":[OSD([subQ0])]})});}
            var Q1;
            {var subQ1=sQuery(id+"F23.wireOp",EDGE,"E58.0");Q1=makeQuery(id+"F24.boolean.opBoolean","SPLIT",FACE,{"disambiguationData":[TD([makeQuery(id+"F15.opExtrude","SWEPT_FACE",FACE,{"disambiguationData":[OSD([sQuery(id+"F14.wireOp",EDGE,"E40")])]})])],"derivedFrom":makeQuery(id+"F24.opExtrude","SWEPT_FACE",FACE,{"disambiguationData":[OSD([subQ1])]})});}
            var Q2;
            {var subQ1=sQuery(id+"F23.wireOp",EDGE,"E58.1");Q2=makeQuery(id+"F24.boolean.opBoolean","SPLIT",FACE,{"disambiguationData":[TD([makeQuery(id+"F15.opExtrude","SWEPT_FACE",FACE,{"disambiguationData":[OSD([sQuery(id+"F14.wireOp",EDGE,"E41.MirrorCS")])]})])],"derivedFrom":makeQuery(id+"F24.opExtrude","SWEPT_FACE",FACE,{"disambiguationData":[OSD([subQ1])]})});}
            var Q3;
            {var subQ2=sQuery(id+"F23.wireOp",EDGE,"E58.0");Q3=makeQuery(id+"F24.boolean.opBoolean","SPLIT",FACE,{"disambiguationData":[TD([makeQuery(id+"F15.opExtrude","SWEPT_FACE",FACE,{"disambiguationData":[OSD([sQuery(id+"F14.wireOp",EDGE,"E41.MirrorCS")])]})])],"derivedFrom":makeQuery(id+"F24.opExtrude","SWEPT_FACE",FACE,{"disambiguationData":[OSD([subQ2])]})});}
            extrude(context, id + "F25", {"entities" : qUnion([Q0, Q1, Q2, Q3]), "operationType" : NewBodyOperationType.REMOVE, "oppositeDirection" : true, "depth" : 25 * mm, "offsetDistance" : 25 * mm});
        }
        {
            var Q0;
            {var subQ0=makeQuery(id+"F17.opExtrude","SWEPT_FACE",FACE,{"disambiguationData":[OSD([sQuery(id+"F16.wireOp",EDGE,"E48.0.9")])]});Q0=makeQuery(id+"F22.opBoolean","MERGE",FACE,{"derivedFrom":[subQ0,makeQuery(id+"F19.boolean.opBoolean","MERGE",FACE,{"derivedFrom":[makeQuery(id+"F15.opExtrude","SWEPT_FACE",FACE,{"disambiguationData":[OSD([sQuery(id+"F14.wireOp",EDGE,"E39")])]}),makeQuery(id+"F19.opExtrude","SWEPT_FACE",FACE,{"disambiguationData":[OSD([sQuery(id+"F18.wireOp",EDGE,"E53")])]})]}),makeQuery(id+"F20.opPattern","COPY",FACE,{"derivedFrom":subQ0,"instanceName":"1"})]});}
            var sketch = newSketch(context, id + "F26", { "sketchPlane" : qUnion([Q0])});
            skCircle(sketch, "E60", {"center": v(0, -22.7) * mm, "radius": 18.5 * mm});
            skPoint(sketch, "E60.centerSnap0", {"position": v(-20, -22.7) * mm});
            skCircle(sketch, "E61", {"center": v(-16, -6.7) * mm, "radius": 1.45 * mm});
            skCircle(sketch, "E62.MirrorC", {"center": v(16, -6.7) * mm, "radius": 1.45 * mm});
            skLineSegment(sketch, "E63", {"start": v(-20, -22.7) * mm, "end": v(20, -22.7) * mm, "construction": true});
            skCircle(sketch, "E64.MirrorC", {"center": v(-16, -38.7) * mm, "radius": 1.45 * mm});
            skCircle(sketch, "E65.MirrorC", {"center": v(16, -38.7) * mm, "radius": 1.45 * mm});
            skCircle(sketch, "E66", {"center": v(-16, -6.7) * mm, "radius": 4 * mm, "construction": true});
            skSolve(sketch);
        }
        {
            var Q0;
            Q0 = qSketchRegion(id + "F26", true);
            extrude(context, id + "F27", {"entities" : qUnion([Q0]), "operationType" : NewBodyOperationType.REMOVE, "oppositeDirection" : true, "depth" : 1.2 * mm, "offsetDistance" : 25 * mm});
        }
        {
            var Q0;
            Q0=makeQuery(id+"F26.imprint","IMPRINT",FACE,{"disambiguationData":[TD([[makeQuery(id+"F26.imprint","IMPRINT",EDGE,{"derivedFrom":sQuery(id+"F26.wireOp",EDGE,"E61")}),1.0]])]});
            var Q1;
            Q1=makeQuery(id+"F26.imprint","IMPRINT",FACE,{"disambiguationData":[TD([[makeQuery(id+"F26.imprint","IMPRINT",EDGE,{"derivedFrom":sQuery(id+"F26.wireOp",EDGE,"E62.MirrorC")}),-1.0]])]});
            var Q2;
            Q2=makeQuery(id+"F26.imprint","IMPRINT",FACE,{"disambiguationData":[TD([[makeQuery(id+"F26.imprint","IMPRINT",EDGE,{"derivedFrom":sQuery(id+"F26.wireOp",EDGE,"E64.MirrorC")}),-1.0]])]});
            var Q3;
            Q3=makeQuery(id+"F26.imprint","IMPRINT",FACE,{"disambiguationData":[TD([[makeQuery(id+"F26.imprint","IMPRINT",EDGE,{"derivedFrom":sQuery(id+"F26.wireOp",EDGE,"E65.MirrorC")}),1.0]])]});
            extrude(context, id + "F28", {"entities" : qUnion([Q0, Q1, Q2, Q3]), "operationType" : NewBodyOperationType.REMOVE, "oppositeDirection" : true, "depth" : 25 * mm, "offsetDistance" : 25 * mm});
        }
        {
            var Q0;
            Q0=qCreatedBy(makeId("Right.planeOp"),FACE);
            var sketch = newSketch(context, id + "F29", { "sketchPlane" : qUnion([Q0])});
            skLineSegment(sketch, "E67.bottom", {"start": v(7.6, -1.5) * mm, "end": v(12.6, -1.5) * mm});
            skLineSegment(sketch, "E67.top", {"start": v(7.6, -3.7) * mm, "end": v(12.6, -3.7) * mm});
            skLineSegment(sketch, "E67.left", {"start": v(7.6, -1.5) * mm, "end": v(7.6, -3.7) * mm});
            skLineSegment(sketch, "E67.right", {"start": v(12.6, -1.5) * mm, "end": v(12.6, -3.7) * mm});
            skLineSegment(sketch, "E68.bottom", {"start": v(12.6, -1.5) * mm, "end": v(14.6, -1.5) * mm});
            skLineSegment(sketch, "E68.top", {"start": v(12.6, -6.9) * mm, "end": v(14.6, -6.9) * mm});
            skLineSegment(sketch, "E68.left", {"start": v(12.6, -1.5) * mm, "end": v(12.6, -6.9) * mm});
            skLineSegment(sketch, "E68.right", {"start": v(14.6, -1.5) * mm, "end": v(14.6, -6.9) * mm});
            skLineSegment(sketch, "E69.bottom", {"start": v(7.6, -4.7) * mm, "end": v(12.6, -4.7) * mm});
            skLineSegment(sketch, "E69.top", {"start": v(7.6, -6.9) * mm, "end": v(12.6, -6.9) * mm});
            skLineSegment(sketch, "E69.left", {"start": v(7.6, -4.7) * mm, "end": v(7.6, -6.9) * mm});
            skLineSegment(sketch, "E69.right", {"start": v(12.6, -4.7) * mm, "end": v(12.6, -6.9) * mm});
            skSolve(sketch);
        }
        {
            var Q0;
            {var subQ0=sQuery(id+"F29.wireOp",EDGE,"E67.bottom");Q0=makeQuery(id+"F29.imprint","IMPRINT",FACE,{"disambiguationData":[TD([[makeQuery(id+"F29.imprint","IMPRINT",EDGE,{"derivedFrom":subQ0}),-1.0]])]});}
            var Q1;
            Q1=makeQuery(id+"F29.imprint","IMPRINT",FACE,{"disambiguationData":[TD([[makeQuery(id+"F29.imprint","IMPRINT",EDGE,{"derivedFrom":sQuery(id+"F29.wireOp",EDGE,"E69.bottom")}),-1.0]])]});
            extrude(context, id + "F30", {"entities" : qUnion([Q0, Q1]), "endBound" : BoundingType.SYMMETRIC, "depth" : 20 * mm, "offsetDistance" : 25 * mm});
        }
        {
            var Q0;
            {var subQ3=sQuery(id+"F29.wireOp",EDGE,"E68.bottom");Q0=makeQuery(id+"F29.imprint","IMPRINT",FACE,{"disambiguationData":[TD([[makeQuery(id+"F29.imprint","IMPRINT",EDGE,{"derivedFrom":subQ3}),-1.0]])]});}
            extrude(context, id + "F31", {"entities" : qUnion([Q0]), "operationType" : NewBodyOperationType.ADD, "endBound" : BoundingType.SYMMETRIC, "depth" : 40 * mm, "offsetDistance" : 25 * mm});
        }
        {
            var Q0;
            Q0=makeQuery(id+"F31.opExtrude","SWEPT_FACE",FACE,{"disambiguationData":[OSD([sQuery(id+"F29.wireOp",EDGE,"E68.right")])]});
            var sketch = newSketch(context, id + "F32", { "sketchPlane" : qUnion([Q0])});
            skCircle(sketch, "E70", {"center": v(-16.3, -4.2) * mm, "radius": 2.7 * mm, "construction": true});
            skCircle(sketch, "E71", {"center": v(-16.3, -4.2) * mm, "radius": 1.45 * mm});
            skCircle(sketch, "E72.MirrorC", {"center": v(16.3, -4.2) * mm, "radius": 1.45 * mm});
            skSolve(sketch);
        }
        {
            var Q0;
            Q0=qCreatedBy(makeId("Right.planeOp"),FACE);
            var sketch = newSketch(context, id + "F33", { "sketchPlane" : qUnion([Q0])});
            skPoint(sketch, "E73.0", {"position": v(19.6, -1.5) * mm});
            skLineSegment(sketch, "E74.bottom", {"start": v(19.6, -1.5) * mm, "end": v(20.8, -1.5) * mm});
            skLineSegment(sketch, "E74.top", {"start": v(19.6, -54.5) * mm, "end": v(20.8, -54.5) * mm});
            skLineSegment(sketch, "E74.left", {"start": v(19.6, -1.5) * mm, "end": v(19.6, -54.5) * mm});
            skLineSegment(sketch, "E74.right", {"start": v(20.8, -1.5) * mm, "end": v(20.8, -54.5) * mm});
            skLineSegment(sketch, "E75.bottom", {"start": v(13.4, -34.5) * mm, "end": v(12.2, -34.5) * mm});
            skLineSegment(sketch, "E75.top", {"start": v(13.4, -54.5) * mm, "end": v(12.2, -54.5) * mm});
            skLineSegment(sketch, "E75.left", {"start": v(13.4, -34.5) * mm, "end": v(13.4, -54.5) * mm});
            skLineSegment(sketch, "E75.right", {"start": v(12.2, -34.5) * mm, "end": v(12.2, -54.5) * mm});
            skSolve(sketch);
        }
        {
            var Q0;
            Q0 = qSketchRegion(id + "F33", true);
            extrude(context, id + "F34", {"entities" : qUnion([Q0]), "endBound" : BoundingType.SYMMETRIC, "depth" : 40 * mm, "offsetDistance" : 25 * mm});
        }
        {
            var Q0;
            Q0 = qSketchRegion(id + "F32", true);
            extrude(context, id + "F35", {"entities" : qUnion([Q0]), "operationType" : NewBodyOperationType.REMOVE, "endBound" : BoundingType.THROUGH_ALL, "oppositeDirection" : true, "depth" : 25 * mm, "offsetDistance" : 25 * mm, "hasSecondDirection" : true, "secondDirectionBound" : SecondDirectionBoundingType.THROUGH_ALL, "secondDirectionOppositeDirection" : false, "secondDirectionDepth" : 25 * mm});
        }
        {
            var Q0;
            Q0=makeQuery(id+"F34.opExtrude","SWEPT_FACE",FACE,{"disambiguationData":[OSD([sQuery(id+"F33.wireOp",EDGE,"E74.right")])]});
            var sketch = newSketch(context, id + "F36", { "sketchPlane" : qUnion([Q0])});
            skCircle(sketch, "E76", {"center": v(2, -21.5) * mm, "radius": 15 * mm});
            skPoint(sketch, "E76.centerSnap0", {"position": v(2, -1.5) * mm});
            skSolve(sketch);
        }
        {
            var Q0;
            Q0 = qSketchRegion(id + "F36", true);
            extrude(context, id + "F37", {"entities" : qUnion([Q0]), "operationType" : NewBodyOperationType.REMOVE, "endBound" : BoundingType.THROUGH_ALL, "oppositeDirection" : true, "depth" : 25 * mm, "offsetDistance" : 25 * mm});
        }
        {
            var Q0;
            Q0=makeQuery(id+"F34.opExtrude","SWEPT_FACE",FACE,{"disambiguationData":[OSD([sQuery(id+"F33.wireOp",EDGE,"E75.right")])]});
            var sketch = newSketch(context, id + "F38", { "sketchPlane" : qUnion([Q0])});
            skLineSegment(sketch, "E77", {"start": v(-9.14, -52.7) * mm, "end": v(-20, -47.5) * mm});
            skLineSegment(sketch, "E78.0", {"start": v(-10, -54.5) * mm, "end": v(-20, -49.72) * mm});
            skLineSegment(sketch, "E79.bottom", {"start": v(-20, -34.5) * mm, "end": v(-21.2, -34.5) * mm});
            skLineSegment(sketch, "E79.left", {"start": v(-20, -34.5) * mm, "end": v(-20, -49.72) * mm});
            skLineSegment(sketch, "E80.0", {"start": v(-9.14, -51.37) * mm, "end": v(-20, -46.17) * mm});
            skLineSegment(sketch, "E81.0", {"start": v(-10, -55.83) * mm, "end": v(-21.2, -50.47) * mm});
            skLineSegment(sketch, "E82", {"start": v(-9.14, -51.37) * mm, "end": v(-9.14, -52.7) * mm});
            skLineSegment(sketch, "E83", {"start": v(-21.2, -34.5) * mm, "end": v(-21.2, -50.47) * mm});
            skLineSegment(sketch, "E84.MirrorCS", {"start": v(9.14, -51.37) * mm, "end": v(9.14, -52.7) * mm});
            skLineSegment(sketch, "E85.MirrorCS", {"start": v(20, -34.5) * mm, "end": v(21.2, -34.5) * mm});
            skLineSegment(sketch, "E86.MirrorCS", {"start": v(10, -54.5) * mm, "end": v(20, -49.72) * mm});
            skLineSegment(sketch, "E87.MirrorCS", {"start": v(9.14, -51.37) * mm, "end": v(20, -46.17) * mm});
            skLineSegment(sketch, "E88.MirrorCS", {"start": v(10, -55.83) * mm, "end": v(21.2, -50.47) * mm});
            skLineSegment(sketch, "E89.MirrorCS", {"start": v(20, -34.5) * mm, "end": v(20, -49.72) * mm});
            skLineSegment(sketch, "E90.MirrorCS", {"start": v(9.14, -52.7) * mm, "end": v(20, -47.5) * mm});
            skLineSegment(sketch, "E91.MirrorCS", {"start": v(21.2, -34.5) * mm, "end": v(21.2, -50.47) * mm});
            skLineSegment(sketch, "E92.bottom", {"start": v(-10, -54.5) * mm, "end": v(10, -54.5) * mm});
            skLineSegment(sketch, "E92.top", {"start": v(-10, -55.83) * mm, "end": v(10, -55.83) * mm});
            skLineSegment(sketch, "E92.left", {"start": v(-10, -54.5) * mm, "end": v(-10, -55.83) * mm});
            skLineSegment(sketch, "E92.right", {"start": v(10, -54.5) * mm, "end": v(10, -55.83) * mm});
            skLineSegment(sketch, "E93", {"start": v(-20, -46.17) * mm, "end": v(-21.2, -46.17) * mm});
            skLineSegment(sketch, "E94", {"start": v(20, -46.17) * mm, "end": v(21.2, -46.17) * mm});
            skLineSegment(sketch, "E95", {"start": v(-10, -54.5) * mm, "end": v(-9.14, -52.7) * mm});
            skLineSegment(sketch, "E96", {"start": v(9.14, -52.7) * mm, "end": v(10, -54.5) * mm});
            skSolve(sketch);
        }
        {
            var Q0;
            {var subQ8=sQuery(id+"F38.wireOp",EDGE,"E85.MirrorCS");Q0=makeQuery(id+"F38.imprint","IMPRINT",FACE,{"disambiguationData":[TD([[makeQuery(id+"F38.imprint","IMPRINT",EDGE,{"derivedFrom":subQ8}),-1.0]])]});}
            var Q1;
            {var subQ0=sQuery(id+"F38.wireOp",EDGE,"E86.MirrorCS");Q1=makeQuery(id+"F38.imprint","IMPRINT",FACE,{"disambiguationData":[TD([[makeQuery(id+"F38.imprint","IMPRINT",EDGE,{"derivedFrom":subQ0}),-1.0]])]});}
            var Q2;
            {var subQ0=sQuery(id+"F38.wireOp",EDGE,"E78.0");Q2=makeQuery(id+"F38.imprint","IMPRINT",FACE,{"disambiguationData":[TD([[makeQuery(id+"F38.imprint","IMPRINT",EDGE,{"derivedFrom":subQ0}),1.0]])]});}
            var Q3;
            {var subQ6=sQuery(id+"F38.wireOp",EDGE,"E79.bottom");Q3=makeQuery(id+"F38.imprint","IMPRINT",FACE,{"disambiguationData":[TD([[makeQuery(id+"F38.imprint","IMPRINT",EDGE,{"derivedFrom":subQ6}),1.0]])]});}
            var Q4;
            Q4=makeQuery(id+"F38.imprint","IMPRINT",FACE,{"disambiguationData":[TD([[makeQuery(id+"F38.imprint","IMPRINT",EDGE,{"derivedFrom":sQuery(id+"F38.wireOp",EDGE,"E92.top")}),1.0]])]});
            var Q5;
            {var subQ0=sQuery(id+"F38.wireOp",EDGE,"E92.left");Q5=makeQuery(id+"F38.imprint","IMPRINT",FACE,{"disambiguationData":[TD([[makeQuery(id+"F38.imprint","IMPRINT",EDGE,{"derivedFrom":subQ0}),-1.0]])]});}
            var Q6;
            {var subQ0=sQuery(id+"F38.wireOp",EDGE,"E92.right");Q6=makeQuery(id+"F38.imprint","IMPRINT",FACE,{"disambiguationData":[TD([[makeQuery(id+"F38.imprint","IMPRINT",EDGE,{"derivedFrom":subQ0}),1.0]])]});}
            var Q7;
            {var subQ3=sQuery(id+"F38.wireOp",EDGE,"E93");Q7=makeQuery(id+"F38.imprint","IMPRINT",FACE,{"disambiguationData":[TD([[makeQuery(id+"F38.imprint","IMPRINT",EDGE,{"derivedFrom":subQ3}),1.0]])]});}
            var Q8;
            {var subQ3=sQuery(id+"F38.wireOp",EDGE,"E94");Q8=makeQuery(id+"F38.imprint","IMPRINT",FACE,{"disambiguationData":[TD([[makeQuery(id+"F38.imprint","IMPRINT",EDGE,{"derivedFrom":subQ3}),-1.0]])]});}
            extrude(context, id + "F39", {"entities" : qUnion([Q0, Q1, Q2, Q3, Q4, Q5, Q6, Q7, Q8]), "operationType" : NewBodyOperationType.ADD, "oppositeDirection" : true, "depth" : 8.6 * mm, "offsetDistance" : 25 * mm});
        }
        {
            var Q0;
            {var subQ0=sQuery(id+"F38.wireOp",EDGE,"E77");Q0=makeQuery(id+"F38.imprint","IMPRINT",FACE,{"disambiguationData":[TD([[makeQuery(id+"F38.imprint","IMPRINT",EDGE,{"derivedFrom":subQ0}),-1.0]])]});}
            var Q1;
            Q1=makeQuery(id+"F38.imprint","IMPRINT",FACE,{"disambiguationData":[TD([[makeQuery(id+"F38.imprint","IMPRINT",EDGE,{"derivedFrom":sQuery(id+"F38.wireOp",EDGE,"E84.MirrorCS")}),1.0]])]});
            var Q2;
            {var subQ0=sQuery(id+"F38.wireOp",EDGE,"E92.left");Q2=makeQuery(id+"F38.imprint","IMPRINT",FACE,{"disambiguationData":[TD([[makeQuery(id+"F38.imprint","IMPRINT",EDGE,{"derivedFrom":subQ0}),-1.0]])]});}
            var Q3;
            {var subQ0=sQuery(id+"F38.wireOp",EDGE,"E92.right");Q3=makeQuery(id+"F38.imprint","IMPRINT",FACE,{"disambiguationData":[TD([[makeQuery(id+"F38.imprint","IMPRINT",EDGE,{"derivedFrom":subQ0}),1.0]])]});}
            var Q4;
            {var subQ0=sQuery(id+"F38.wireOp",EDGE,"E78.0");Q4=makeQuery(id+"F38.imprint","IMPRINT",FACE,{"disambiguationData":[TD([[makeQuery(id+"F38.imprint","IMPRINT",EDGE,{"derivedFrom":subQ0}),1.0]])]});}
            var Q5;
            {var subQ0=sQuery(id+"F38.wireOp",EDGE,"E86.MirrorCS");Q5=makeQuery(id+"F38.imprint","IMPRINT",FACE,{"disambiguationData":[TD([[makeQuery(id+"F38.imprint","IMPRINT",EDGE,{"derivedFrom":subQ0}),-1.0]])]});}
            var Q6;
            {var subQ3=sQuery(id+"F38.wireOp",EDGE,"E93");Q6=makeQuery(id+"F38.imprint","IMPRINT",FACE,{"disambiguationData":[TD([[makeQuery(id+"F38.imprint","IMPRINT",EDGE,{"derivedFrom":subQ3}),1.0]])]});}
            var Q7;
            {var subQ3=sQuery(id+"F38.wireOp",EDGE,"E94");Q7=makeQuery(id+"F38.imprint","IMPRINT",FACE,{"disambiguationData":[TD([[makeQuery(id+"F38.imprint","IMPRINT",EDGE,{"derivedFrom":subQ3}),-1.0]])]});}
            extrude(context, id + "F40", {"entities" : qUnion([Q0, Q1, Q2, Q3, Q4, Q5, Q6, Q7]), "operationType" : NewBodyOperationType.ADD, "depth" : 24 * mm, "offsetDistance" : 25 * mm});
        }
        {
            var Q0;
            {var subQ0=sQuery(id+"F38.wireOp",EDGE,"E77");Q0=makeQuery(id+"F38.imprint","IMPRINT",FACE,{"disambiguationData":[TD([[makeQuery(id+"F38.imprint","IMPRINT",EDGE,{"derivedFrom":subQ0}),1.0]])]});}
            var Q1;
            {var subQ0=sQuery(id+"F38.wireOp",EDGE,"E86.MirrorCS");Q1=makeQuery(id+"F38.imprint","IMPRINT",FACE,{"disambiguationData":[TD([[makeQuery(id+"F38.imprint","IMPRINT",EDGE,{"derivedFrom":subQ0}),1.0]])]});}
            extrude(context, id + "F41", {"entities" : qUnion([Q0, Q1]), "operationType" : NewBodyOperationType.REMOVE, "oppositeDirection" : true, "depth" : 3 * mm, "offsetDistance" : 25 * mm});
        }
        {
            var Q0;
            {var subQ0=sQuery(id+"F38.wireOp",EDGE,"E81.0");var subQ1=sQuery(id+"F33.wireOp",EDGE,"E75.right");var subQ4=makeQuery(id+"F34.opExtrude","CAP_EDGE",EDGE,{"disambiguationData":[OSD([subQ1])],"isStart":true});var subQ5=makeQuery(id+"F38.imprint","INTERSECT",VERTEX,{"derivedFrom":[subQ4,subQ0]});Q0=makeQuery(id+"F38.imprint","IMPRINT",FACE,{"disambiguationData":[TD([[makeQuery(id+"F38.imprint","IMPRINT",EDGE,{"disambiguationData":[TD([[subQ5,1.0]])],"derivedFrom":subQ0}),1.0]])]});}
            var Q1;
            {var subQ0=sQuery(id+"F38.wireOp",EDGE,"E88.MirrorCS");var subQ1=sQuery(id+"F33.wireOp",EDGE,"E75.right");var subQ4=makeQuery(id+"F34.opExtrude","CAP_EDGE",EDGE,{"disambiguationData":[OSD([subQ1])],"isStart":false});var subQ5=makeQuery(id+"F38.imprint","INTERSECT",VERTEX,{"derivedFrom":[subQ4,subQ0]});Q1=makeQuery(id+"F38.imprint","IMPRINT",FACE,{"disambiguationData":[TD([[makeQuery(id+"F38.imprint","IMPRINT",EDGE,{"disambiguationData":[TD([[subQ5,1.0]])],"derivedFrom":subQ0}),-1.0]])]});}
            extrude(context, id + "F42", {"entities" : qUnion([Q0, Q1]), "operationType" : NewBodyOperationType.REMOVE, "endBound" : BoundingType.THROUGH_ALL, "oppositeDirection" : true, "depth" : 25 * mm, "offsetDistance" : 25 * mm});
        }
        {
            var Q0;
            Q0=makeQuery(id+"F40.opExtrude","CAP_FACE",FACE,{"disambiguationData":[OSD([sQuery(id+"F38.wireOp",EDGE,"E77"),sQuery(id+"F38.wireOp",EDGE,"E78.0"),sQuery(id+"F38.wireOp",EDGE,"E79.left"),sQuery(id+"F38.wireOp",EDGE,"E80.0"),sQuery(id+"F38.wireOp",EDGE,"E81.0"),sQuery(id+"F38.wireOp",EDGE,"E82"),sQuery(id+"F38.wireOp",EDGE,"E83"),sQuery(id+"F38.wireOp",EDGE,"E92.left"),sQuery(id+"F38.wireOp",EDGE,"E93")])],"isStart":false});
            var sketch = newSketch(context, id + "F43", { "sketchPlane" : qUnion([Q0])});
            skLineSegment(sketch, "E97.0.0", {"start": v(-9.14, -52.7) * mm, "end": v(-9.14, -51.37) * mm});
            skLineSegment(sketch, "E97.0.1", {"start": v(-9.14, -51.37) * mm, "end": v(-20, -46.17) * mm});
            skLineSegment(sketch, "E98.0.0", {"start": v(-20, -46.17) * mm, "end": v(-21.2, -46.17) * mm});
            skLineSegment(sketch, "E98.0.1", {"start": v(-21.2, -46.17) * mm, "end": v(-21.2, -50.47) * mm});
            skLineSegment(sketch, "E98.0.2", {"start": v(-21.2, -50.47) * mm, "end": v(-20, -51.05) * mm});
            skLineSegment(sketch, "E99.0.0", {"start": v(-20, -51.05) * mm, "end": v(-12.78, -54.5) * mm});
            skLineSegment(sketch, "E100.0.2", {"start": v(-12.78, -54.5) * mm, "end": v(-10, -55.83) * mm});
            skLineSegment(sketch, "E101", {"start": v(-9.14, -52.7) * mm, "end": v(-10, -55.83) * mm});
            skLineSegment(sketch, "E102.MirrorCS", {"start": v(21.2, -50.47) * mm, "end": v(20, -51.05) * mm});
            skLineSegment(sketch, "E103.MirrorCS", {"start": v(20, -46.17) * mm, "end": v(21.2, -46.17) * mm});
            skLineSegment(sketch, "E104.MirrorCS", {"start": v(20, -51.05) * mm, "end": v(12.78, -54.5) * mm});
            skLineSegment(sketch, "E105.MirrorCS", {"start": v(9.14, -52.7) * mm, "end": v(9.14, -51.37) * mm});
            skLineSegment(sketch, "E106.MirrorCS", {"start": v(9.14, -51.37) * mm, "end": v(20, -46.17) * mm});
            skLineSegment(sketch, "E107.MirrorCS", {"start": v(21.2, -46.17) * mm, "end": v(21.2, -50.47) * mm});
            skLineSegment(sketch, "E108.MirrorCS", {"start": v(12.78, -54.5) * mm, "end": v(10, -55.83) * mm});
            skLineSegment(sketch, "E109.MirrorCS", {"start": v(9.14, -52.7) * mm, "end": v(10, -55.83) * mm});
            skSolve(sketch);
        }
        {
            var Q0;
            Q0 = qSketchRegion(id + "F43", true);
            extrude(context, id + "F44", {"entities" : qUnion([Q0]), "operationType" : NewBodyOperationType.ADD, "depth" : 1.2 * mm, "offsetDistance" : 25 * mm});
        }
        {
            var Q0;
            Q0=makeQuery(id+"F3.opExtrude","CAP_EDGE",EDGE,{"disambiguationData":[OSD([sQuery(id+"F2.wireOp",EDGE,"E12")])],"isStart":false});
            var Q1;
            Q1=makeQuery(id+"F3.opExtrude","CAP_EDGE",EDGE,{"disambiguationData":[OSD([sQuery(id+"F2.wireOp",EDGE,"E13.right")])],"isStart":false});
            var Q2;
            Q2=makeQuery(id+"F3.opExtrude","CAP_EDGE",EDGE,{"disambiguationData":[OSD([sQuery(id+"F2.wireOp",EDGE,"E15.MirrorCS")])],"isStart":false});
            var Q3;
            Q3=makeQuery(id+"F3.opExtrude","CAP_EDGE",EDGE,{"disambiguationData":[OSD([sQuery(id+"F2.wireOp",EDGE,"E15.MirrorCS")])],"isStart":true});
            var Q4;
            Q4=makeQuery(id+"F3.opExtrude","CAP_EDGE",EDGE,{"disambiguationData":[OSD([sQuery(id+"F2.wireOp",EDGE,"E12")])],"isStart":true});
            var Q5;
            Q5=makeQuery(id+"F3.opExtrude","CAP_EDGE",EDGE,{"disambiguationData":[OSD([sQuery(id+"F2.wireOp",EDGE,"E13.right")])],"isStart":true});
            chamfer(context, id + "F45", {"entities" : qUnion([Q0, Q1, Q2, Q3, Q4, Q5]), "width" : 0.7 * mm, "tangentPropagation" : true});
        }
    });
